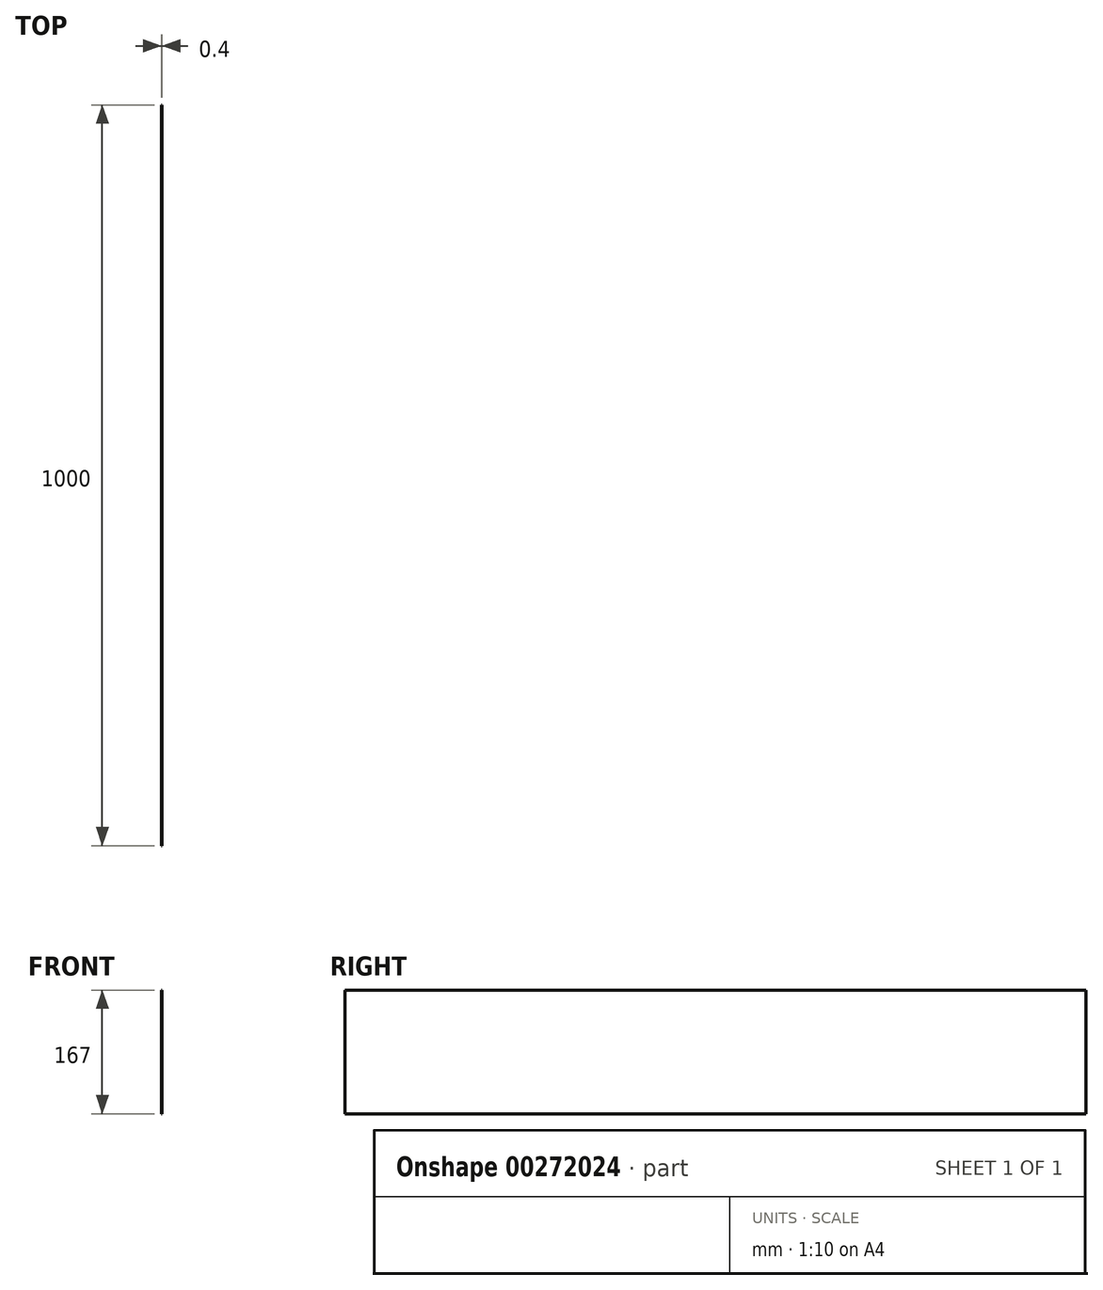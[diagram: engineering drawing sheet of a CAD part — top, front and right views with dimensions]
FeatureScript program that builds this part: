
annotation { "Feature Type Name" : "Feature", "Feature Type Description" : "" }
export const myFeature = defineFeature(function(context is Context, id is Id, definition is map)
    precondition{}
    {
        {
            var Q0;
            Q0=qCreatedBy(makeId("Front.planeOp"),FACE);
            var sketch = newSketch(context, id + "F0", { "sketchPlane" : qUnion([Q0])});
            skLineSegment(sketch, "E0.bottom", {"start": v(0.2, 83.5) * mm, "end": v(-0.2, 83.5) * mm});
            skLineSegment(sketch, "E0.top", {"start": v(0.2, -83.5) * mm, "end": v(-0.2, -83.5) * mm});
            skLineSegment(sketch, "E0.left", {"start": v(0.2, 83.5) * mm, "end": v(0.2, -83.5) * mm});
            skLineSegment(sketch, "E0.right", {"start": v(-0.2, 83.5) * mm, "end": v(-0.2, -83.5) * mm});
            skPoint(sketch, "E0.middle", {"position": v(0, 0) * mm});
            skSolve(sketch);
        }
        {
            var Q0;
            Q0 = qSketchRegion(id + "F0", true);
            extrude(context, id + "F1", {"entities" : qUnion([Q0]), "endBound" : BoundingType.SYMMETRIC, "depth" : 1000 * mm});
        }
    });
